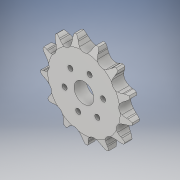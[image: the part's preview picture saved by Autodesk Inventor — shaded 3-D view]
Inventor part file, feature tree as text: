
AUTODESK INVENTOR PART (.ipt)
format: ipt  version: 2019 (Build 230136000, 136)  size: 416,256 bytes
history: mixed  units: in
note: dims shown in document units (in); Inventor stores cm internally (conversion verified against a paired STEP export)
features: sketch x2, hole x1, other x1, imported_body x1
ambient origin geometry x8: Origin, YZ Plane, XZ Plane, XY Plane, X Axis, Y Axis, Z Axis, Center Point
bodies: Solid1 (imported_parasolid)
feature tree (5):
  sketch  "Sketch1"  dims[d0=1.5in d1=60.0deg]
  hole  "Hole1"  [1 undecoded]
  sketch  "Sketch2"  dims[d2=60.0deg d3=0.1935in d4=0.75in d5=0.375in d6=0.25in d7=0.5635in d8=1.0in d9=0.8108in]
  other  "Cut-Extrude2"
  imported_body  NMx_Import_Brep_tag  [imported B-rep: ~14 faces, bbox_mm=[42.048684, 36.155842, 11.6586]]
note: 1 required parameter value undecoded (feature->parameter linkage not recoverable at this tier; creation-order binding heuristic only, values carry confidence <= 0.55)
